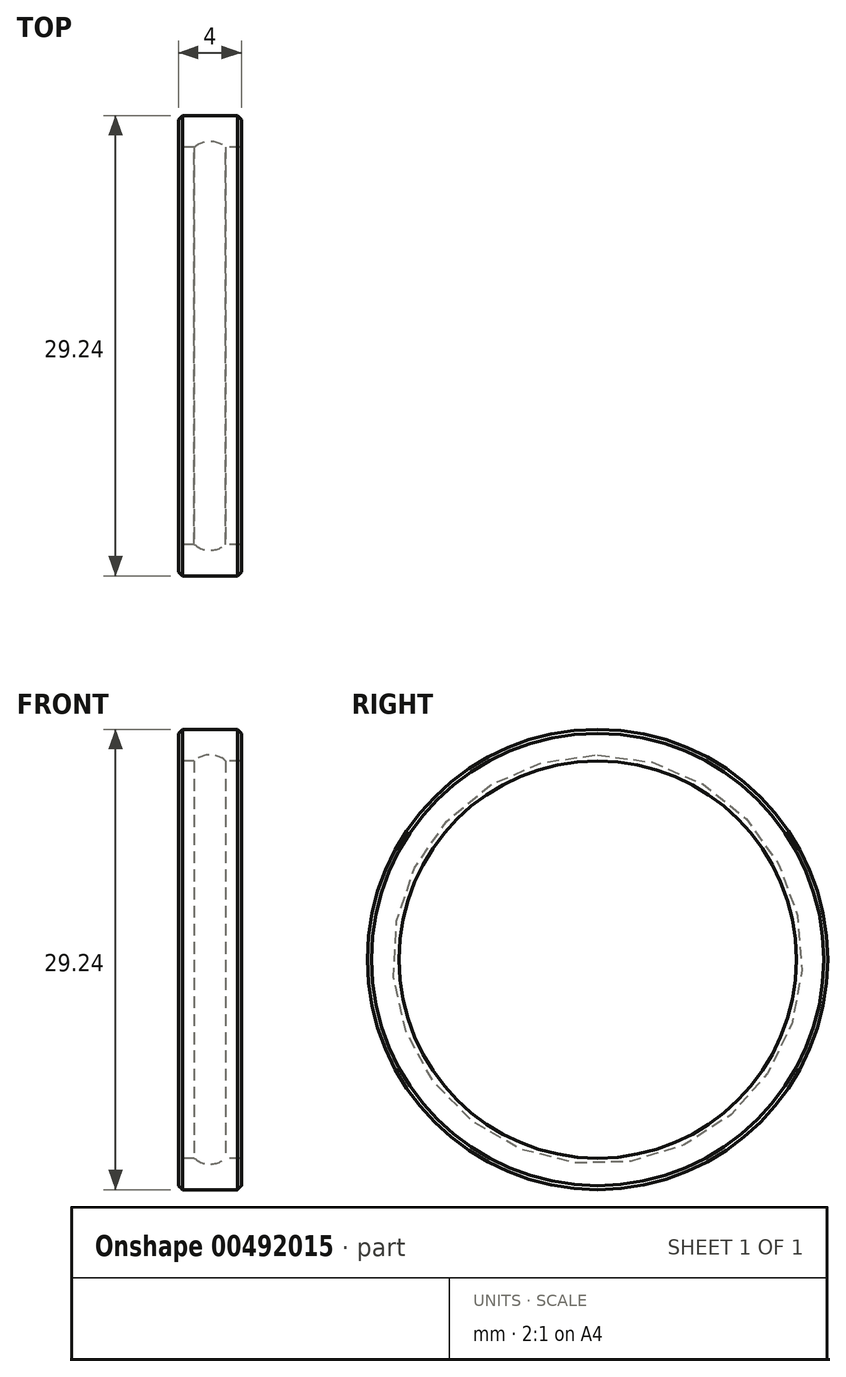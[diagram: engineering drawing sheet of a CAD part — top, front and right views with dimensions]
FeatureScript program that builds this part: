
annotation { "Feature Type Name" : "Feature", "Feature Type Description" : "" }
export const myFeature = defineFeature(function(context is Context, id is Id, definition is map)
    precondition{}
    {
        {
            var Q0;
            Q0=qCreatedBy(makeId("Front.planeOp"),FACE);
            var sketch = newSketch(context, id + "F0", { "sketchPlane" : qUnion([Q0])});
            skArc(sketch, "E0", {"start": v(1, 12.62) * mm, "mid": v(0.54, 12.9) * mm, "end": v(0, 13) * mm});
            skLineSegment(sketch, "E1.bottom", {"start": v(0, 13) * mm, "end": v(0, 13) * mm});
            skLineSegment(sketch, "E1.top", {"start": v(0, 14.62) * mm, "end": v(0, 14.62) * mm});
            skLineSegment(sketch, "E1.left", {"start": v(0, 13) * mm, "end": v(0, 14.62) * mm});
            skLineSegment(sketch, "E1.right", {"start": v(0, 13) * mm, "end": v(0, 14.62) * mm, "construction": true});
            skLineSegment(sketch, "E2", {"start": v(0, 14.62) * mm, "end": v(2, 14.62) * mm});
            skLineSegment(sketch, "E3", {"start": v(2, 14.62) * mm, "end": v(2, 12.62) * mm});
            skLineSegment(sketch, "E4", {"start": v(2, 12.62) * mm, "end": v(1, 12.62) * mm});
            skPoint(sketch, "E5", {"position": v(1, 14.62) * mm});
            skLineSegment(sketch, "E6.MirrorCS", {"start": v(-2, 12.62) * mm, "end": v(-1, 12.62) * mm});
            skArc(sketch, "E7.MirrorCS", {"start": v(-1, 12.62) * mm, "mid": v(-0.54, 12.9) * mm, "end": v(0, 13) * mm});
            skLineSegment(sketch, "E8.MirrorCS", {"start": v(0, 14.62) * mm, "end": v(-2, 14.62) * mm});
            skPoint(sketch, "E9.MirrorP", {"position": v(-1, 14.62) * mm});
            skLineSegment(sketch, "E10.MirrorCS", {"start": v(-2, 14.62) * mm, "end": v(-2, 12.62) * mm});
            skLineSegment(sketch, "E11", {"start": v(-3.36, 0) * mm, "end": v(4.18, 0) * mm, "construction": true});
            skSolve(sketch);
        }
        {
            var Q0;
            Q0=makeQuery(id+"F0.imprint","IMPRINT",FACE,{"disambiguationData":[TD([[makeQuery(id+"F0.imprint","IMPRINT",EDGE,{"derivedFrom":sQuery(id+"F0.wireOp",EDGE,"E0")}),-1.0]])]});
            var Q1;
            Q1=makeQuery(id+"F0.imprint","IMPRINT",FACE,{"disambiguationData":[TD([[makeQuery(id+"F0.imprint","IMPRINT",EDGE,{"derivedFrom":sQuery(id+"F0.wireOp",EDGE,"E6.MirrorCS")}),1.0]])]});
            var Q2;
            Q2=sQuery(id+"F0.wireOp",EDGE,"E11");
            revolve(context, id + "F1", {"entities" : qUnion([Q0, Q1]), "axis" : qUnion([Q2]), "revolveType" : RevolveType.FULL});
        }
        {
            var Q0;
            Q0=makeQuery(id+"F1.opRevolve","SWEPT_EDGE",EDGE,{"disambiguationData":[OSD([sQuery(id+"F0.wireOp",EDGE,"E2"),sQuery(id+"F0.wireOp",EDGE,"E3")])]});
            var Q1;
            Q1=makeQuery(id+"F1.opRevolve","SWEPT_EDGE",EDGE,{"disambiguationData":[OSD([sQuery(id+"F0.wireOp",EDGE,"E8.MirrorCS"),sQuery(id+"F0.wireOp",EDGE,"E10.MirrorCS")])]});
            chamfer(context, id + "F2", {"entities" : qUnion([Q0, Q1]), "width" : .25 * mm, "tangentPropagation" : true});
        }
    });
